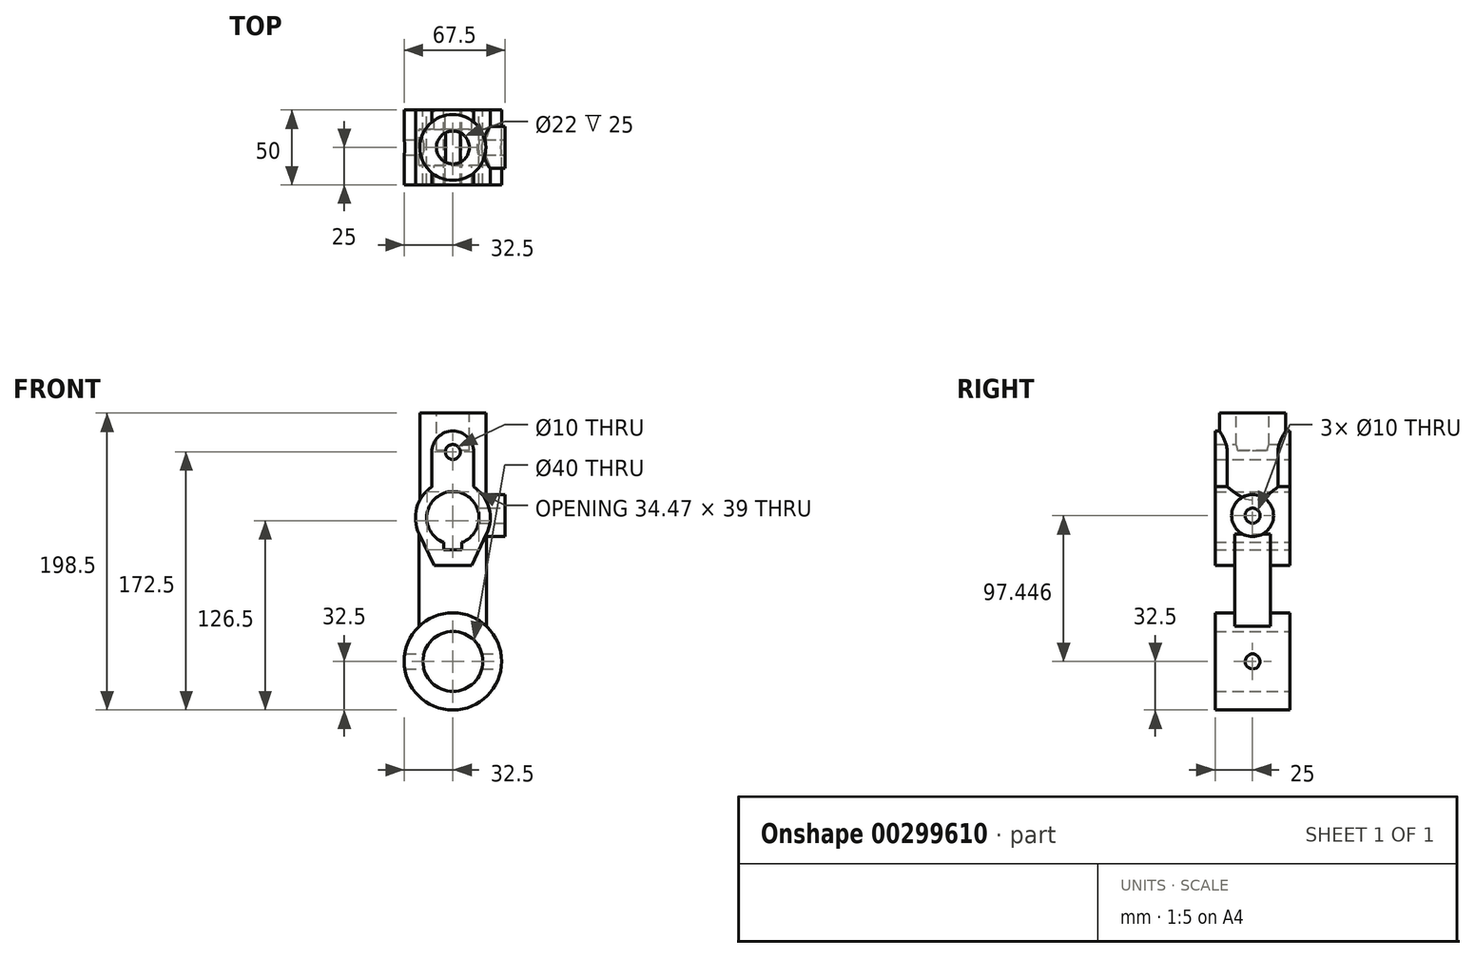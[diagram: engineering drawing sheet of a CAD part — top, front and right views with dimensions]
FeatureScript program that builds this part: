
annotation { "Feature Type Name" : "Feature", "Feature Type Description" : "" }
export const myFeature = defineFeature(function(context is Context, id is Id, definition is map)
    precondition{}
    {
        {
            var Q0;
            Q0=qCreatedBy(makeId("Front.planeOp"),FACE);
            var sketch = newSketch(context, id + "F0", { "sketchPlane" : qUnion([Q0])});
            skCircle(sketch, "E0", {"center": v(0, 0) * mm, "radius": 32.5 * mm});
            skLineSegment(sketch, "E1", {"start": v(-22.5, 23.45) * mm, "end": v(-22.5, 85.1) * mm});
            skArc(sketch, "E2", {"start": v(22.6, 85.3) * mm, "mid": v(24.11, 102.6) * mm, "end": v(14, 116.71) * mm});
            skLineSegment(sketch, "E3", {"start": v(-14, 116.71) * mm, "end": v(-14, 140) * mm});
            skLineSegment(sketch, "E4", {"start": v(14, 116.71) * mm, "end": v(14, 140) * mm});
            skArc(sketch, "E5", {"start": v(14, 140) * mm, "mid": v(0, 154) * mm, "end": v(-14, 140) * mm});
            skLineSegment(sketch, "E6", {"start": v(22.5, 85.1) * mm, "end": v(22.5, 23.45) * mm});
            skCircle(sketch, "E7", {"center": v(0, 0) * mm, "radius": 20 * mm});
            skCircle(sketch, "E8", {"center": v(0, 140) * mm, "radius": 5 * mm});
            skArc(sketch, "E9", {"start": v(6, 79.56) * mm, "mid": v(0, 113.5) * mm, "end": v(-6, 79.56) * mm});
            skLineSegment(sketch, "E10", {"start": v(-6, 79.56) * mm, "end": v(-6, 74.5) * mm});
            skLineSegment(sketch, "E11", {"start": v(-6, 74.5) * mm, "end": v(6, 74.5) * mm});
            skLineSegment(sketch, "E12", {"start": v(6, 74.5) * mm, "end": v(6, 79.56) * mm});
            skArc(sketch, "E13.trimOffspring", {"start": v(-14, 116.71) * mm, "mid": v(-24.11, 102.6) * mm, "end": v(-22.6, 85.3) * mm});
            skLineSegment(sketch, "E14", {"start": v(-22.6, 85.3) * mm, "end": v(-12.5, 64) * mm});
            skLineSegment(sketch, "E15", {"start": v(22.6, 85.3) * mm, "end": v(12.5, 64) * mm});
            skLineSegment(sketch, "E16", {"start": v(-12.5, 64) * mm, "end": v(12.5, 64) * mm});
            skLineSegment(sketch, "E17", {"start": v(-22.5, 106.9) * mm, "end": v(-22.5, 166) * mm});
            skLineSegment(sketch, "E18", {"start": v(-22.5, 166) * mm, "end": v(22.5, 166) * mm});
            skLineSegment(sketch, "E19", {"start": v(22.5, 166) * mm, "end": v(22.5, 106.9) * mm});
            skSolve(sketch);
        }
        {
            var Q0;
            Q0=makeQuery(id+"F0.imprint","IMPRINT",FACE,{"disambiguationData":[TD([[makeQuery(id+"F0.imprint","IMPRINT",EDGE,{"derivedFrom":sQuery(id+"F0.wireOp",EDGE,"E7")}),-1.0]])]});
            var Q1;
            {var subQ6=sQuery(id+"F0.wireOp",EDGE,"E2");Q1=makeQuery(id+"F0.imprint","IMPRINT",FACE,{"disambiguationData":[TD([[makeQuery(id+"F0.imprint","IMPRINT",EDGE,{"derivedFrom":subQ6}),1.0]])]});}
            extrude(context, id + "F1", {"entities" : qUnion([Q0, Q1]), "endBound" : BoundingType.SYMMETRIC, "depth" : 50 * mm});
        }
        {
            var Q0;
            Q0=qCreatedBy(makeId("Top.planeOp"),FACE);
            cPlane(context, id + "F2", {"entities" : qUnion([Q0]), "cplaneType" : CPlaneType.OFFSET, "offset" : 166 * mm, "width" : 150 * mm, "height" : 150 * mm});
        }
        {
            var Q0;
            Q0=qCreatedBy(id+"F2.planeOp",FACE);
            var sketch = newSketch(context, id + "F3", { "sketchPlane" : qUnion([Q0])});
            skCircle(sketch, "E20", {"center": v(0, 0) * mm, "radius": 22 * mm});
            skCircle(sketch, "E21", {"center": v(0, 0) * mm, "radius": 11 * mm});
            skSolve(sketch);
        }
        {
            var Q0;
            {var subQ0=sQuery(id+"F0.wireOp",EDGE,"E16");Q0=makeQuery(id+"F0.imprint","IMPRINT",FACE,{"disambiguationData":[TD([[makeQuery(id+"F0.imprint","IMPRINT",EDGE,{"derivedFrom":subQ0}),-1.0]])]});}
            extrude(context, id + "F4", {"entities" : qUnion([Q0]), "operationType" : NewBodyOperationType.ADD, "endBound" : BoundingType.SYMMETRIC, "depth" : 24 * mm});
        }
        {
            var Q0;
            Q0 = qSketchRegion(id + "F3", true);
            extrude(context, id + "F5", {"entities" : qUnion([Q0]), "operationType" : NewBodyOperationType.ADD, "oppositeDirection" : true, "depth" : 59.6 * mm});
        }
        {
            var Q0;
            Q0=makeQuery(id+"F0.imprint","IMPRINT",FACE,{"disambiguationData":[TD([[makeQuery(id+"F0.imprint","IMPRINT",EDGE,{"derivedFrom":sQuery(id+"F0.wireOp",EDGE,"E9")}),1.0]])]});
            extrude(context, id + "F6", {"entities" : qUnion([Q0]), "operationType" : NewBodyOperationType.REMOVE, "endBound" : BoundingType.SYMMETRIC, "oppositeDirection" : true, "depth" : 70.4 * mm});
        }
        {
            var Q0;
            Q0=makeQuery(id+"F1.opExtrude","CAP_FACE",FACE,{"disambiguationData":[OSD([sQuery(id+"F0.wireOp",EDGE,"E2"),sQuery(id+"F0.wireOp",EDGE,"E3"),sQuery(id+"F0.wireOp",EDGE,"E4"),sQuery(id+"F0.wireOp",EDGE,"E5"),sQuery(id+"F0.wireOp",EDGE,"E8"),sQuery(id+"F0.wireOp",EDGE,"E9"),sQuery(id+"F0.wireOp",EDGE,"E10"),sQuery(id+"F0.wireOp",EDGE,"E11"),sQuery(id+"F0.wireOp",EDGE,"E12"),sQuery(id+"F0.wireOp",EDGE,"E13.trimOffspring"),sQuery(id+"F0.wireOp",EDGE,"E14"),sQuery(id+"F0.wireOp",EDGE,"E15"),sQuery(id+"F0.wireOp",EDGE,"E16")])],"isStart":false});
            var sketch = newSketch(context, id + "F7", { "sketchPlane" : qUnion([Q0])});
            skSolve(sketch);
        }
        {
            var Q0;
            Q0=makeQuery(id+"F7.imprint","IMPRINT",FACE,{"disambiguationData":[TD([[makeQuery(id+"F7.imprint","IMPRINT",EDGE,{"derivedFrom":makeQuery(id+"F1.opExtrude","CAP_EDGE",EDGE,{"disambiguationData":[OSD([sQuery(id+"F0.wireOp",EDGE,"E8")])],"isStart":false})}),1.0]])]});
            var Q1;
            Q1=sQuery(id+"F0.wireOp",EDGE,"E8");
            extrude(context, id + "F8", {"entities" : qUnion([Q0]), "operationType" : NewBodyOperationType.REMOVE, "surfaceEntities" : qUnion([Q1]), "endBound" : BoundingType.THROUGH_ALL, "oppositeDirection" : true, "depth" : 74.2 * mm});
        }
        {
            var Q0;
            Q0=qCreatedBy(makeId("Right.planeOp"),FACE);
            cPlane(context, id + "F9", {"entities" : qUnion([Q0]), "cplaneType" : CPlaneType.OFFSET, "offset" : 35 * mm, "width" : 150 * mm, "height" : 150 * mm});
        }
        {
            var Q0;
            Q0=qCreatedBy(id+"F9.planeOp",FACE);
            var sketch = newSketch(context, id + "F10", { "sketchPlane" : qUnion([Q0])});
            skCircle(sketch, "E22", {"center": v(0, 97.45) * mm, "radius": 14 * mm});
            skCircle(sketch, "E23", {"center": v(0, 97.45) * mm, "radius": 5 * mm});
            skSolve(sketch);
        }
        {
            var Q0;
            Q0=makeQuery(id+"F10.imprint","IMPRINT",FACE,{"disambiguationData":[TD([[makeQuery(id+"F10.imprint","IMPRINT",EDGE,{"derivedFrom":sQuery(id+"F10.wireOp",EDGE,"E22")}),1.0]])]});
            extrude(context, id + "F11", {"entities" : qUnion([Q0]), "operationType" : NewBodyOperationType.ADD, "oppositeDirection" : true, "depth" : 13.9 * mm});
        }
        {
            var Q0;
            Q0=qCreatedBy(makeId("Right.planeOp"),FACE);
            cPlane(context, id + "F12", {"entities" : qUnion([Q0]), "cplaneType" : CPlaneType.OFFSET, "offset" : 32.6 * mm, "width" : 150 * mm, "height" : 150 * mm});
        }
        {
            var Q0;
            Q0=qCreatedBy(id+"F12.planeOp",FACE);
            var sketch = newSketch(context, id + "F13", { "sketchPlane" : qUnion([Q0])});
            skCircle(sketch, "E24", {"center": v(0, 0) * mm, "radius": 5 * mm});
            skSolve(sketch);
        }
        {
            var Q0;
            Q0 = qSketchRegion(id + "F13", true);
            extrude(context, id + "F14", {"entities" : qUnion([Q0]), "operationType" : NewBodyOperationType.REMOVE, "endBound" : BoundingType.THROUGH_ALL, "oppositeDirection" : true, "depth" : 25 * mm});
        }
        {
            var Q0;
            Q0=makeQuery(id+"F11.opExtrude","CAP_FACE",FACE,{"disambiguationData":[OSD([sQuery(id+"F10.wireOp",EDGE,"E22"),sQuery(id+"F10.wireOp",EDGE,"E23")])],"isStart":true});
            var sketch = newSketch(context, id + "F15", { "sketchPlane" : qUnion([Q0])});
            skSolve(sketch);
        }
        {
            var Q0;
            Q0=makeQuery(id+"F3.imprint","IMPRINT",FACE,{"disambiguationData":[TD([[makeQuery(id+"F3.imprint","IMPRINT",EDGE,{"derivedFrom":sQuery(id+"F3.wireOp",EDGE,"E21")}),1.0]])]});
            extrude(context, id + "F16", {"entities" : qUnion([Q0]), "operationType" : NewBodyOperationType.REMOVE, "oppositeDirection" : true, "depth" : 25 * mm});
        }
        {
            var Q0;
            Q0=makeQuery(id+"F15.imprint","IMPRINT",FACE,{"disambiguationData":[TD([[makeQuery(id+"F15.imprint","IMPRINT",EDGE,{"derivedFrom":makeQuery(id+"F11.opExtrude","CAP_EDGE",EDGE,{"disambiguationData":[OSD([sQuery(id+"F10.wireOp",EDGE,"E23")])],"isStart":true})}),1.0]])]});
            extrude(context, id + "F17", {"entities" : qUnion([Q0]), "operationType" : NewBodyOperationType.REMOVE, "oppositeDirection" : true, "depth" : 25 * mm});
        }
    });
